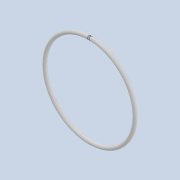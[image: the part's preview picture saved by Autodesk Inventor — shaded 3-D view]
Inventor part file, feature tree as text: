
AUTODESK INVENTOR PART (.ipt)
format: ipt  version: 2020.4 (Build 244396000, 396)  size: 141,312 bytes
history: native  units: mm
features: sketch x3, sweep x1, extrude x1
ambient origin geometry x8: Origin, YZ Plane, XZ Plane, XY Plane, X Axis, Y Axis, Z Axis, Center Point
bodies: Solid1 (feature_tree)
feature tree (5):
  sweep  "Sweep1"
  extrude  "Extrusion1"  Depth=2.0mm
  sketch  "Sketch1"  dims[d0=40.8mm d1=1.65mm]
  sketch  "Sketch2"  dims[d2=0.0mm d3=0.0mm d4=2.0mm]
  sketch  "Sketch3"  dims[d5=0.75mm d6=0.0mm]
